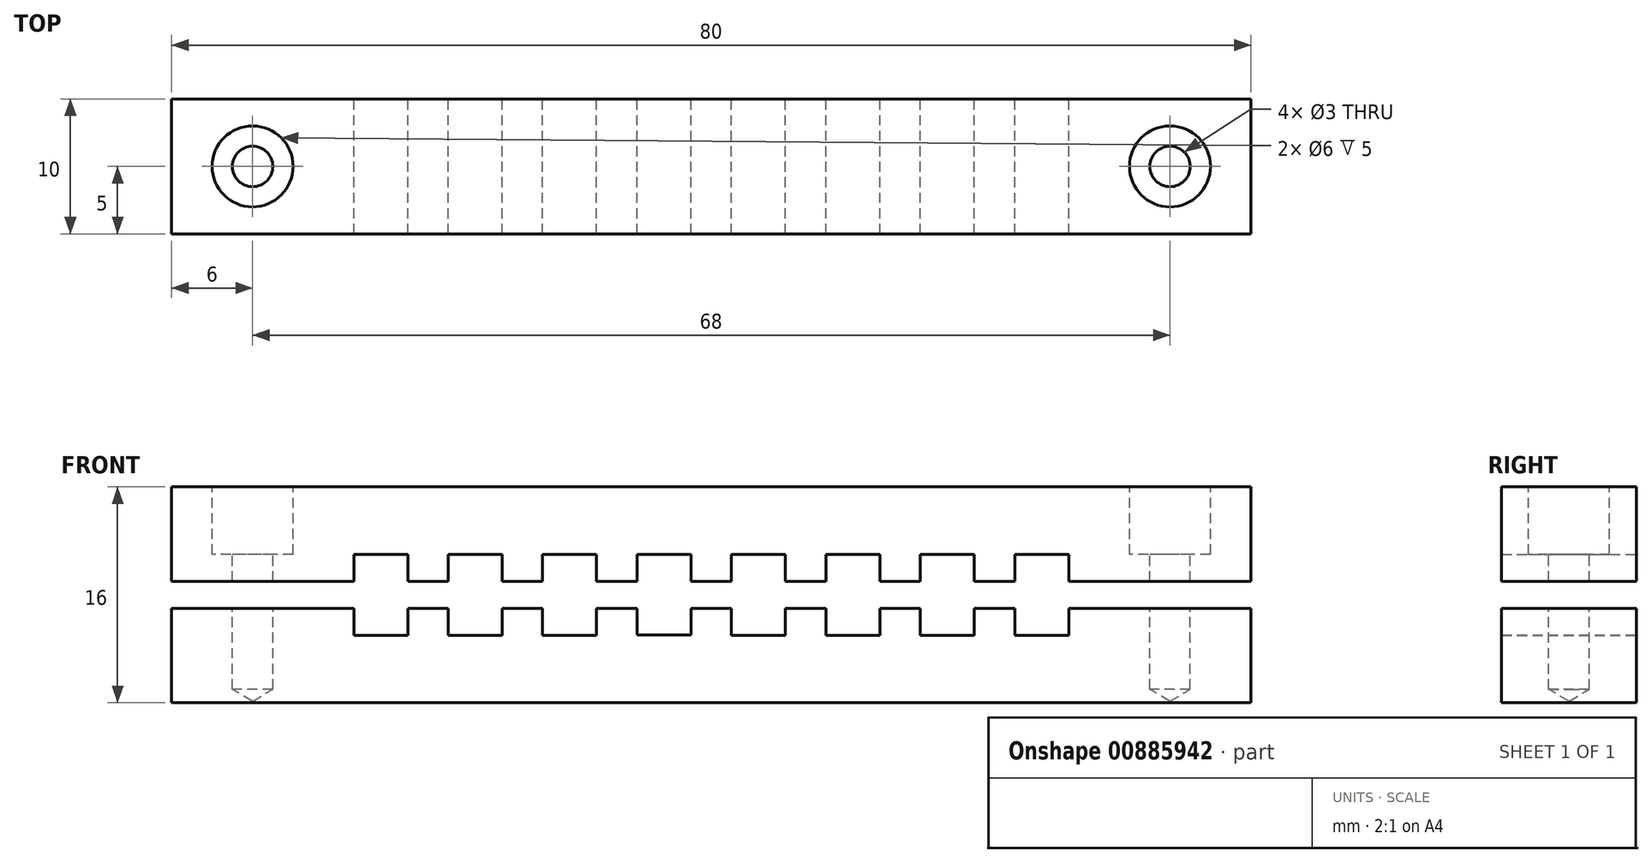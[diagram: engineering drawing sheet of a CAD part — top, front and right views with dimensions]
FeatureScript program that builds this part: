
annotation { "Feature Type Name" : "Feature", "Feature Type Description" : "" }
export const myFeature = defineFeature(function(context is Context, id is Id, definition is map)
    precondition{}
    {
        {
            var Q0;
            Q0=qCreatedBy(makeId("Front.planeOp"),FACE);
            var sketch = newSketch(context, id + "F0", { "sketchPlane" : qUnion([Q0])});
            skLineSegment(sketch, "E0.bottom", {"start": v(0, 0) * mm, "end": v(80, 0) * mm});
            skLineSegment(sketch, "E0.top", {"start": v(0, 7) * mm, "end": v(80, 7) * mm});
            skLineSegment(sketch, "E0.left", {"start": v(0, 0) * mm, "end": v(0, 7) * mm});
            skLineSegment(sketch, "E0.right", {"start": v(80, 0) * mm, "end": v(80, 7) * mm});
            skLineSegment(sketch, "E1.bottom", {"start": v(13.5, 7) * mm, "end": v(17.5, 7) * mm});
            skLineSegment(sketch, "E1.top", {"start": v(13.5, 5) * mm, "end": v(17.5, 5) * mm});
            skLineSegment(sketch, "E1.left", {"start": v(13.5, 7) * mm, "end": v(13.5, 5) * mm});
            skLineSegment(sketch, "E1.right", {"start": v(17.5, 7) * mm, "end": v(17.5, 5) * mm});
            skLineSegment(sketch, "E2.top", {"start": v(20.5, 5) * mm, "end": v(24.5, 5) * mm});
            skLineSegment(sketch, "E2.left", {"start": v(20.5, 7) * mm, "end": v(20.5, 5) * mm});
            skLineSegment(sketch, "E2.right", {"start": v(24.5, 7) * mm, "end": v(24.5, 5) * mm});
            skLineSegment(sketch, "E3.top", {"start": v(27.5, 5) * mm, "end": v(31.5, 5) * mm});
            skLineSegment(sketch, "E3.left", {"start": v(27.5, 7) * mm, "end": v(27.5, 5) * mm});
            skLineSegment(sketch, "E3.right", {"start": v(31.5, 7) * mm, "end": v(31.5, 5) * mm});
            skLineSegment(sketch, "E4.top", {"start": v(34.5, 5.01) * mm, "end": v(38.5, 5.01) * mm});
            skLineSegment(sketch, "E4.left", {"start": v(34.5, 7.01) * mm, "end": v(34.5, 5.01) * mm});
            skLineSegment(sketch, "E4.right", {"start": v(38.5, 7.01) * mm, "end": v(38.5, 5.01) * mm});
            skLineSegment(sketch, "E5.top", {"start": v(41.5, 5) * mm, "end": v(45.5, 5) * mm});
            skLineSegment(sketch, "E5.left", {"start": v(41.5, 7) * mm, "end": v(41.5, 5) * mm});
            skLineSegment(sketch, "E5.right", {"start": v(45.5, 7) * mm, "end": v(45.5, 5) * mm});
            skLineSegment(sketch, "E6.top", {"start": v(48.5, 5) * mm, "end": v(52.5, 5) * mm});
            skLineSegment(sketch, "E6.left", {"start": v(48.5, 7) * mm, "end": v(48.5, 5) * mm});
            skLineSegment(sketch, "E6.right", {"start": v(52.5, 7) * mm, "end": v(52.5, 5) * mm});
            skLineSegment(sketch, "E7.top", {"start": v(62.5, 5) * mm, "end": v(66.5, 5) * mm});
            skLineSegment(sketch, "E7.left", {"start": v(62.5, 7) * mm, "end": v(62.5, 5) * mm});
            skLineSegment(sketch, "E7.right", {"start": v(66.5, 7) * mm, "end": v(66.5, 5) * mm});
            skLineSegment(sketch, "E8.top", {"start": v(55.5, 5) * mm, "end": v(59.5, 5) * mm});
            skLineSegment(sketch, "E8.left", {"start": v(55.5, 7) * mm, "end": v(55.5, 5) * mm});
            skLineSegment(sketch, "E8.right", {"start": v(59.5, 7) * mm, "end": v(59.5, 5) * mm});
            skLineSegment(sketch, "E9", {"start": v(0, 8) * mm, "end": v(79.95, 8) * mm, "construction": true});
            skLineSegment(sketch, "E10.MirrorCS", {"start": v(13.5, 9) * mm, "end": v(13.5, 11) * mm});
            skLineSegment(sketch, "E11.MirrorCS", {"start": v(17.5, 9) * mm, "end": v(17.5, 11) * mm});
            skLineSegment(sketch, "E12.MirrorCS", {"start": v(55.5, 9) * mm, "end": v(55.5, 11) * mm});
            skLineSegment(sketch, "E13.MirrorCS", {"start": v(41.5, 9) * mm, "end": v(41.5, 11) * mm});
            skLineSegment(sketch, "E14.MirrorCS", {"start": v(52.5, 9) * mm, "end": v(52.5, 11) * mm});
            skLineSegment(sketch, "E15.MirrorCS", {"start": v(27.5, 9) * mm, "end": v(27.5, 11) * mm});
            skLineSegment(sketch, "E16.MirrorCS", {"start": v(48.5, 9) * mm, "end": v(48.5, 11) * mm});
            skLineSegment(sketch, "E17.MirrorCS", {"start": v(66.5, 9) * mm, "end": v(66.5, 11) * mm});
            skLineSegment(sketch, "E18.MirrorCS", {"start": v(45.5, 9) * mm, "end": v(45.5, 11) * mm});
            skLineSegment(sketch, "E19.MirrorCS", {"start": v(62.5, 9) * mm, "end": v(62.5, 11) * mm});
            skLineSegment(sketch, "E20.MirrorCS", {"start": v(38.5, 8.99) * mm, "end": v(38.5, 10.99) * mm});
            skLineSegment(sketch, "E21.MirrorCS", {"start": v(24.5, 9) * mm, "end": v(24.5, 11) * mm});
            skLineSegment(sketch, "E22.MirrorCS", {"start": v(34.5, 8.99) * mm, "end": v(34.5, 10.99) * mm});
            skLineSegment(sketch, "E23.MirrorCS", {"start": v(31.5, 9) * mm, "end": v(31.5, 11) * mm});
            skLineSegment(sketch, "E24.MirrorCS", {"start": v(59.5, 9) * mm, "end": v(59.5, 11) * mm});
            skLineSegment(sketch, "E25.MirrorCS", {"start": v(20.5, 9) * mm, "end": v(20.5, 11) * mm});
            skLineSegment(sketch, "E26.MirrorCS", {"start": v(55.5, 11) * mm, "end": v(59.5, 11) * mm});
            skLineSegment(sketch, "E27.MirrorCS", {"start": v(80, 16) * mm, "end": v(80, 9) * mm});
            skLineSegment(sketch, "E28.MirrorCS", {"start": v(41.5, 11) * mm, "end": v(45.5, 11) * mm});
            skLineSegment(sketch, "E29.MirrorCS", {"start": v(0, 16) * mm, "end": v(0, 9) * mm});
            skLineSegment(sketch, "E30.MirrorCS", {"start": v(13.5, 11) * mm, "end": v(17.5, 11) * mm});
            skLineSegment(sketch, "E31.MirrorCS", {"start": v(48.5, 11) * mm, "end": v(52.5, 11) * mm});
            skLineSegment(sketch, "E32.MirrorCS", {"start": v(62.5, 11) * mm, "end": v(66.5, 11) * mm});
            skLineSegment(sketch, "E33.MirrorCS", {"start": v(13.5, 9) * mm, "end": v(17.5, 9) * mm});
            skLineSegment(sketch, "E34.MirrorCS", {"start": v(0, 9) * mm, "end": v(80, 9) * mm});
            skLineSegment(sketch, "E35.MirrorCS", {"start": v(0, 16) * mm, "end": v(80, 16) * mm});
            skLineSegment(sketch, "E36.MirrorCS", {"start": v(27.5, 11) * mm, "end": v(31.5, 11) * mm});
            skLineSegment(sketch, "E37.MirrorCS", {"start": v(20.5, 11) * mm, "end": v(24.5, 11) * mm});
            skLineSegment(sketch, "E38.MirrorCS", {"start": v(34.5, 10.99) * mm, "end": v(38.5, 10.99) * mm});
            skLineSegment(sketch, "E39.bottom", {"start": v(0, 0) * mm, "end": v(79.94, 0) * mm});
            skLineSegment(sketch, "E39.top", {"start": v(0, -14) * mm, "end": v(79.94, -14) * mm});
            skLineSegment(sketch, "E39.left", {"start": v(0, 0) * mm, "end": v(0, -14) * mm});
            skLineSegment(sketch, "E39.right", {"start": v(79.94, 0) * mm, "end": v(79.94, -14) * mm});
            skSolve(sketch);
        }
        {
            var Q0;
            {var subQ18=sQuery(id+"F0.wireOp",EDGE,"E10.MirrorCS");Q0=makeQuery(id+"F0.imprint","IMPRINT",FACE,{"disambiguationData":[TD([[makeQuery(id+"F0.imprint","IMPRINT",EDGE,{"derivedFrom":subQ18}),1.0]])]});}
            var Q1;
            Q1=makeQuery(id+"F0.imprint","IMPRINT",FACE,{"disambiguationData":[TD([[makeQuery(id+"F0.imprint","IMPRINT",EDGE,{"derivedFrom":sQuery(id+"F0.wireOp",EDGE,"E0.bottom")}),1.0]])]});
            extrude(context, id + "F1", {"entities" : qUnion([Q0, Q1]), "depth" : 10 * mm, "offsetDistance" : 25 * mm});
        }
        {
            var Q0;
            Q0=makeQuery(id+"F1.opExtrude","SWEPT_FACE",FACE,{"disambiguationData":[OSD([sQuery(id+"F0.wireOp",EDGE,"E35.MirrorCS")])]});
            var sketch = newSketch(context, id + "F2", { "sketchPlane" : qUnion([Q0])});
            skPoint(sketch, "E40", {"position": v(6, -5) * mm});
            skPoint(sketch, "E40.positionSnap0", {"position": v(0, -5) * mm});
            skPoint(sketch, "E41", {"position": v(74, -5) * mm});
            skSolve(sketch);
        }
        {
            var Q0;
            Q0=sQuery(id+"F2.wireOp",VERTEX,"E40");
            var Q1;
            Q1=sQuery(id+"F2.wireOp",VERTEX,"E41");
            var Q2;
            Q2=makeQuery(id+"F1.opExtrude","SWEPT_BODY",BODY,{"disambiguationData":[OSD([sQuery(id+"F0.wireOp",EDGE,"E0.bottom"),sQuery(id+"F0.wireOp",EDGE,"E0.top"),sQuery(id+"F0.wireOp",EDGE,"E0.left"),sQuery(id+"F0.wireOp",EDGE,"E0.right"),sQuery(id+"F0.wireOp",EDGE,"E1.top"),sQuery(id+"F0.wireOp",EDGE,"E1.left"),sQuery(id+"F0.wireOp",EDGE,"E1.right"),sQuery(id+"F0.wireOp",EDGE,"E2.top"),sQuery(id+"F0.wireOp",EDGE,"E2.left"),sQuery(id+"F0.wireOp",EDGE,"E2.right"),sQuery(id+"F0.wireOp",EDGE,"E3.top"),sQuery(id+"F0.wireOp",EDGE,"E3.left"),sQuery(id+"F0.wireOp",EDGE,"E3.right"),sQuery(id+"F0.wireOp",EDGE,"E4.top"),sQuery(id+"F0.wireOp",EDGE,"E4.left"),sQuery(id+"F0.wireOp",EDGE,"E4.right"),sQuery(id+"F0.wireOp",EDGE,"E5.top"),sQuery(id+"F0.wireOp",EDGE,"E5.left"),sQuery(id+"F0.wireOp",EDGE,"E5.right"),sQuery(id+"F0.wireOp",EDGE,"E6.top"),sQuery(id+"F0.wireOp",EDGE,"E6.left"),sQuery(id+"F0.wireOp",EDGE,"E6.right"),sQuery(id+"F0.wireOp",EDGE,"E7.top"),sQuery(id+"F0.wireOp",EDGE,"E7.left"),sQuery(id+"F0.wireOp",EDGE,"E7.right"),sQuery(id+"F0.wireOp",EDGE,"E8.top"),sQuery(id+"F0.wireOp",EDGE,"E8.left"),sQuery(id+"F0.wireOp",EDGE,"E8.right")])]});
            var Q3;
            Q3=makeQuery(id+"F1.opExtrude","SWEPT_BODY",BODY,{"disambiguationData":[OSD([sQuery(id+"F0.wireOp",EDGE,"E10.MirrorCS"),sQuery(id+"F0.wireOp",EDGE,"E11.MirrorCS"),sQuery(id+"F0.wireOp",EDGE,"E12.MirrorCS"),sQuery(id+"F0.wireOp",EDGE,"E13.MirrorCS"),sQuery(id+"F0.wireOp",EDGE,"E14.MirrorCS"),sQuery(id+"F0.wireOp",EDGE,"E15.MirrorCS"),sQuery(id+"F0.wireOp",EDGE,"E16.MirrorCS"),sQuery(id+"F0.wireOp",EDGE,"E17.MirrorCS"),sQuery(id+"F0.wireOp",EDGE,"E18.MirrorCS"),sQuery(id+"F0.wireOp",EDGE,"E19.MirrorCS"),sQuery(id+"F0.wireOp",EDGE,"E20.MirrorCS"),sQuery(id+"F0.wireOp",EDGE,"E21.MirrorCS"),sQuery(id+"F0.wireOp",EDGE,"E22.MirrorCS"),sQuery(id+"F0.wireOp",EDGE,"E23.MirrorCS"),sQuery(id+"F0.wireOp",EDGE,"E24.MirrorCS"),sQuery(id+"F0.wireOp",EDGE,"E25.MirrorCS"),sQuery(id+"F0.wireOp",EDGE,"E26.MirrorCS"),sQuery(id+"F0.wireOp",EDGE,"E27.MirrorCS"),sQuery(id+"F0.wireOp",EDGE,"E28.MirrorCS"),sQuery(id+"F0.wireOp",EDGE,"E29.MirrorCS"),sQuery(id+"F0.wireOp",EDGE,"E30.MirrorCS"),sQuery(id+"F0.wireOp",EDGE,"E31.MirrorCS"),sQuery(id+"F0.wireOp",EDGE,"E32.MirrorCS"),sQuery(id+"F0.wireOp",EDGE,"E34.MirrorCS"),sQuery(id+"F0.wireOp",EDGE,"E35.MirrorCS"),sQuery(id+"F0.wireOp",EDGE,"E36.MirrorCS"),sQuery(id+"F0.wireOp",EDGE,"E37.MirrorCS"),sQuery(id+"F0.wireOp",EDGE,"E38.MirrorCS")])]});
            hole(context, id + "F3", {"style" : HoleStyle.C_BORE, "endStyle" : HoleEndStyle.BLIND, "holeDiameter" : 3 * mm, "cBoreDiameter" : 6 * mm, "cBoreDepth" : 5 * mm, "majorDiameter" : 5 * mm, "holeDepth" : 15 * mm, "isTappedThrough" : true, "tappedDepth" : 12 * mm, "tapClearance" : 3, "locations" : qUnion([Q0, Q1]), "scope" : qUnion([Q2, Q3])});
        }
    });
